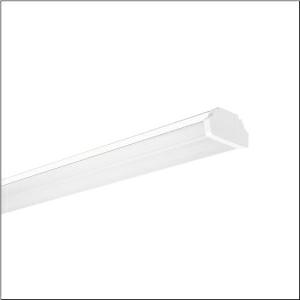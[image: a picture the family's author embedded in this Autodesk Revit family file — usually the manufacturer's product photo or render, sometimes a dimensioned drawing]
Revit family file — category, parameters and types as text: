
# Revit family: modario_31_gen_2_53bm812cv49xc2_7681
name_source: partatom
category: Lighting Fixtures
units: mm (PartAtom-declared; Revit-internal decimal feet)

## family parameters
Cut with Voids When Loaded = No
Host = Face
Light Source = No
Part Type = Normal
Room Calculation Point = No
Round Connector Dimension = Use Diameter
Shared = No

## types (1)
- --- (1 x LED, 9240 lm, 49.9 W, 4000K)
    Apparent Load = 50 VA
    CIE Flux Codes = 47 80 95 93 100
    Color Rendering = 80
    Color Temperature = 4000K
    Default Elevation = 1800 mm
    Description = Modario 31 Gen.2, luminaire insert, of sheet steel, coil coated, white, length: 1.495mm, width: 81mm, height: 82mm, 5x system unit, system units: 299mm, LED rated luminous flux: 9.240lm, light colour: 840, SDCM (Standard Deviation of Colour Matching)MacAdam ≤ 3 SDCM (initial), control gear: ON/OFF Multilumen, CLOi, with plug, 3-pole, with phase selection, mains connection: 220..240V, AC, 50/60Hz, start of lifetime: 50W, end of service life: 61W, through-wiring accessed according to module size, primary optical cover: cover, of PMMA, light emission: direct distribution, primary light characteristic: symmetric, protection rating (complete): IP20, protection rating (LED compartment): IP50, insulation class (complete): insulation class I (protective earthing), certification: CE, ENEC, VDE, UKCA, impact resistance: IK03, permissible ambient temperature for indoor applications: -35..+40°C, corresponds to IFS (International Featured Standards) requirements for safety and quality in the food industry, reducing of maximum allowable ambient temperature of 5°C with ceiling mounting, IP40 when using the optional accessory 5TP9018, packaging unit: 1 piece
    Height = 92 mm
    Lamp = 1 x LED
    Lamp Light Flux = 9240 lm
    Lamp Power = 49.9 W
    Lamp count = 1
    Length = 1495 mm
    Luminous efficacy = 185 lm/W
    Manufacturer = Siteco
    ModVariant = No
    Model = 53BM812CV49XC2
    Mounting Place = Ceiling
    Mounting Type = Pendant
    Number of Poles = 1
    OnlyDefault = Yes
    Power Factor = 1
    Product Name = Modario 31 Gen.2
    Product group = luminaire insert | ceiling pendant
    ProductGroupID = 901
    Protection Class = Protection class I
    Protection Degree = IP 20
    RLX_Detail_Level = 1
    RLX_Emergency_Light_Flux = 0 lm
    RLX_Emergency_Type = 0
    RLX_Emergency_Type_DB = No
    RlxData = <blob elided: 39889 chars, md5=6a94f828>
    Socket = socket
    Standby Power = 0 W
    System Light Flux = 9240 lm
    System Power = 50 W
    Type Comments = factory setting: luminous flux: 100 % | (A | C | E) | 116 mA
    Type Image = l_1341886.jpg
    URL = http://relux.com
    VarID = @adj_052347
    Voltage = 0 V
    Weight = 0.00 kg
    Width = 81 mm

## geometry (parser evidence)
native form markers: Blend x4, Sweep x11
no freeform markers — native parametric forms only
